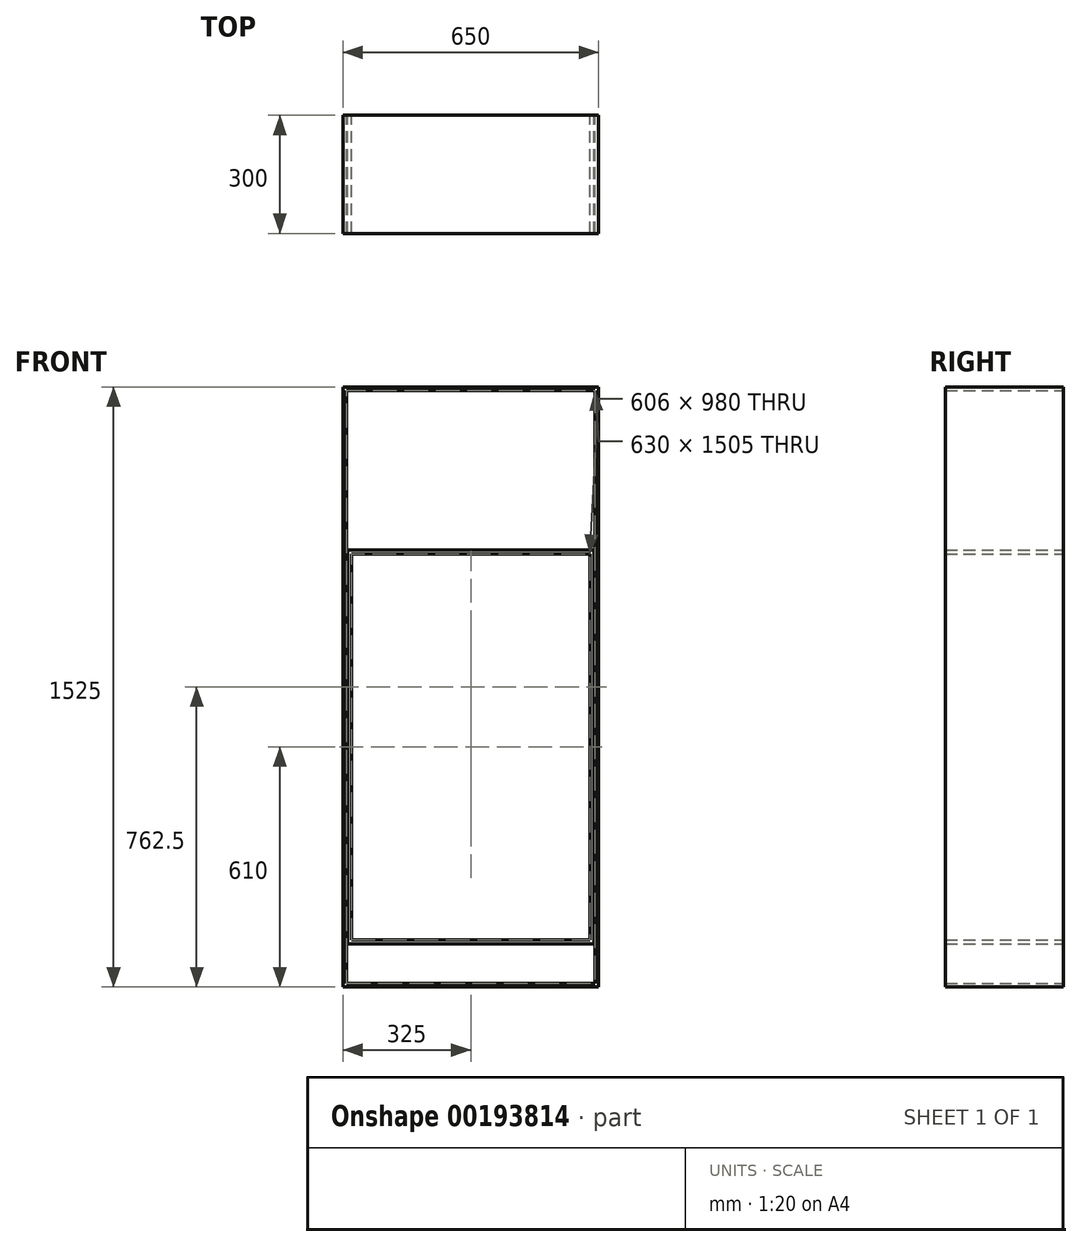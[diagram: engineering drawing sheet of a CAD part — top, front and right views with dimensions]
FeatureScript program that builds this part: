
annotation { "Feature Type Name" : "Feature", "Feature Type Description" : "" }
export const myFeature = defineFeature(function(context is Context, id is Id, definition is map)
    precondition{}
    {
        {
            var Q0;
            Q0=qCreatedBy(makeId("Front.planeOp"),FACE);
            var sketch = newSketch(context, id + "F0", { "sketchPlane" : qUnion([Q0])});
            skLineSegment(sketch, "E0.bottom", {"start": v(325, -762.5) * mm, "end": v(-325, -762.5) * mm});
            skLineSegment(sketch, "E0.top", {"start": v(325, 762.5) * mm, "end": v(-325, 762.5) * mm});
            skLineSegment(sketch, "E0.left", {"start": v(325, -762.5) * mm, "end": v(325, 762.5) * mm});
            skLineSegment(sketch, "E0.right", {"start": v(-325, -762.5) * mm, "end": v(-325, 762.5) * mm});
            skPoint(sketch, "E0.middle", {"position": v(0, 0) * mm});
            skLineSegment(sketch, "E1.0", {"start": v(315, 752.5) * mm, "end": v(-315, 752.5) * mm});
            skLineSegment(sketch, "E1.1", {"start": v(315, -752.5) * mm, "end": v(315, 752.5) * mm});
            skLineSegment(sketch, "E1.2", {"start": v(315, -752.5) * mm, "end": v(-315, -752.5) * mm});
            skLineSegment(sketch, "E1.3", {"start": v(-315, -752.5) * mm, "end": v(-315, 752.5) * mm});
            skSolve(sketch);
        }
        {
            var Q0;
            Q0 = qSketchRegion(id + "F0", true);
            extrude(context, id + "F1", {"entities" : qUnion([Q0]), "depth" : 300 * mm});
        }
        {
            var Q0;
            Q0=qCreatedBy(makeId("Front.planeOp"),FACE);
            var sketch = newSketch(context, id + "F2", { "sketchPlane" : qUnion([Q0])});
            skLineSegment(sketch, "E2", {"start": v(0, 752.5) * mm, "end": v(0, -752.5) * mm, "construction": true});
            skLineSegment(sketch, "E3.bottom", {"start": v(313, -652.5) * mm, "end": v(-313, -652.5) * mm});
            skLineSegment(sketch, "E3.top", {"start": v(313, 347.5) * mm, "end": v(-313, 347.5) * mm});
            skLineSegment(sketch, "E3.left", {"start": v(313, -652.5) * mm, "end": v(313, 347.5) * mm});
            skLineSegment(sketch, "E3.right", {"start": v(-313, -652.5) * mm, "end": v(-313, 347.5) * mm});
            skPoint(sketch, "E3.middle", {"position": v(0, -152.5) * mm});
            skLineSegment(sketch, "E4.0", {"start": v(303, -642.5) * mm, "end": v(-303, -642.5) * mm});
            skLineSegment(sketch, "E4.1", {"start": v(303, -642.5) * mm, "end": v(303, 337.5) * mm});
            skLineSegment(sketch, "E4.2", {"start": v(303, 337.5) * mm, "end": v(-303, 337.5) * mm});
            skLineSegment(sketch, "E4.3", {"start": v(-303, -642.5) * mm, "end": v(-303, 337.5) * mm});
            skSolve(sketch);
        }
        {
            var Q0;
            Q0 = qSketchRegion(id + "F2", true);
            var Q1;
            Q1=makeQuery(id+"F1.opExtrude","CAP_VERTEX",VERTEX,{"disambiguationData":[OSD([sQuery(id+"F0.wireOp",EDGE,"E0.top"),sQuery(id+"F0.wireOp",EDGE,"E0.right")])],"isStart":false});
            extrude(context, id + "F3", {"entities" : qUnion([Q0]), "endBound" : BoundingType.UP_TO_VERTEX, "endBoundEntityVertex" : qUnion([Q1]), "depth" : 25 * mm});
        }
    });
